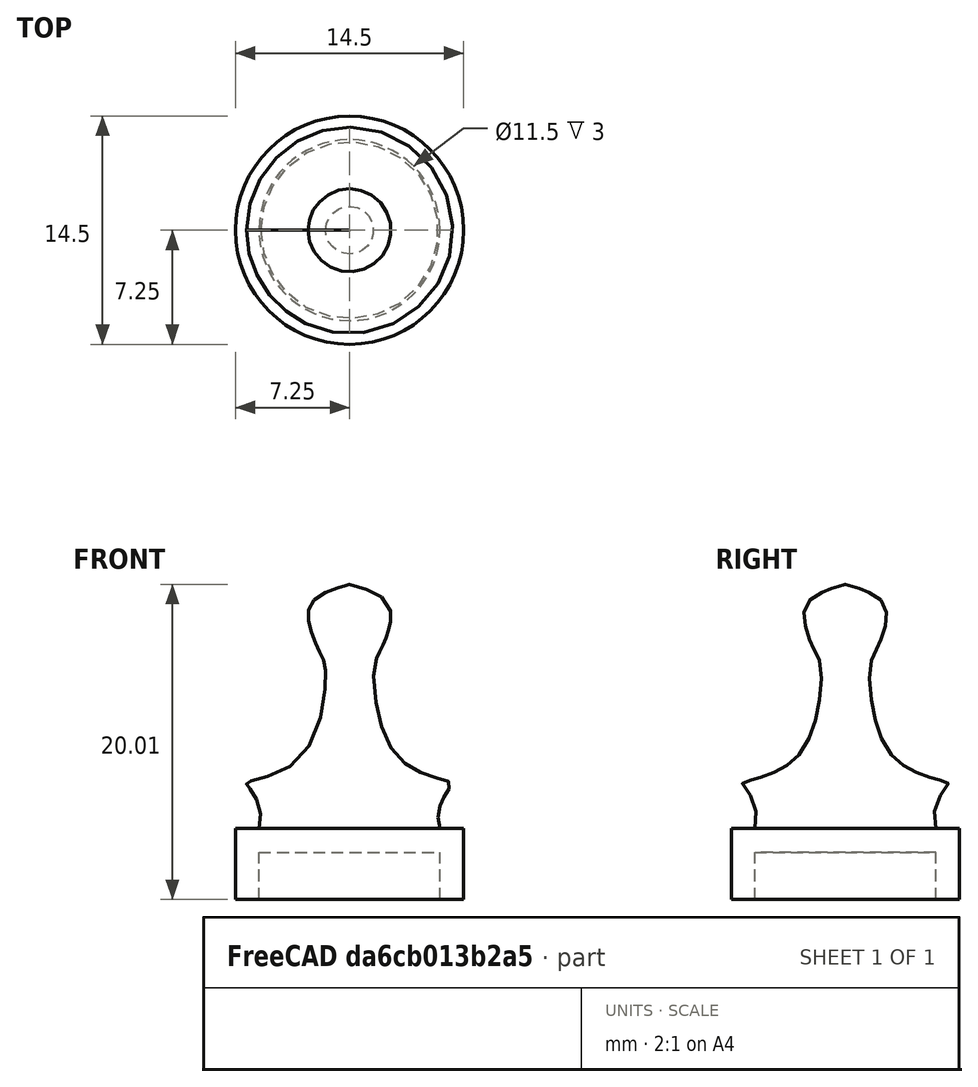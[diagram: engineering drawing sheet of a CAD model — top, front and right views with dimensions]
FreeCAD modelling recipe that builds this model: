
FCSTD DOCUMENT  (FreeCAD 0.21R33771 (Git))
Label: population unit
License: All rights reserved
LicenseURL: http://en.wikipedia.org/wiki/All_rights_reserved
objects: Sketcher::SketchObject×1, PartDesign::Revolution×1, PartDesign::Body×1
note: 4 computed .brp shape members not serialized (recipe doc carries the construction recipe); baked Part::Feature solids carry a one-line shape summary decoded from their .brp

FEATURE [Sketcher::SketchObject] Sketch
  FullyConstrained = false
  MapMode = 5
  Placement = pos=(0,0,0) rot=(1,0,0;1.5708rad)
  Support = -> [XZ_Plane]
  sketch-geometry (29):
    g0: LineSegment StartX=-5.75 StartY=0 StartZ=0 EndX=-5.75 EndY=3 EndZ=0
    g1: LineSegment StartX=-5.75 StartY=3 StartZ=0 EndX=0 EndY=3 EndZ=0
    g2: LineSegment StartX=-5.75 StartY=0 StartZ=0 EndX=-7.25 EndY=0 EndZ=0
    g3: LineSegment StartX=-7.25 StartY=0 StartZ=0 EndX=-7.25 EndY=4.5 EndZ=0
    g4: LineSegment StartX=-7.25 StartY=4.5 StartZ=0 EndX=-5.75 EndY=4.5 EndZ=0
    g5-g16: Circle x12 (B-spline internal-alignment scaffolding for g17; pole/knot coordinates omitted)
    g17: BSplineCurve PolesCount=12 KnotsCount=10 Degree=3 IsPeriodic=0
    g18-g27: GeomPoint x10 (B-spline internal-alignment scaffolding for g17; pole/knot coordinates omitted)
    g28: LineSegment StartX=0 StartY=20 StartZ=0 EndX=0 EndY=3 EndZ=0
  constraints (39):
    c: PointOnObject(g0,g-1)
    c: Vertical(g0)
    c: DistanceY(g0,g0) = 3
    c: Coincident(g1,g0)
    c: PointOnObject(g1,g-2)
    c: Horizontal(g1)
    c: DistanceX(g1,g1) = 5.75
    c: Coincident(g2,g0)
    c: PointOnObject(g2,g-1)
    c: DistanceX(g2,g2) = 1.5
    c: Coincident(g3,g2)
    c: Vertical(g3)
    c: DistanceY(g3,g3) = 4.5
    c: Coincident(g4,g3)
    c: Horizontal(g4)
    c: DistanceX(g4,g4) = 1.5
    c: Weight(g5) = 1
    c: Coincident(g17,g4)
    c: Equal(g5,g6)
    c: Equal(g5,g7)
    c: Equal(g5,g8)
    c: PointOnObject(g8,g7)
    c: Equal(g5,g9)
    c: Equal(g5,g10)
    c: Equal(g5,g11)
    c: PointOnObject(g11,g10)
    c: Equal(g5,g12)
    c: Equal(g5,g13)
    c: Equal(g5,g14)
    c: PointOnObject(g14,g-2)
    c: Equal(g5,g15)
    c: Coincident(g15,g14)
    c: Equal(g5,g16)
    c: InternalAlignment(g5-g16 -> g17) x12
    c: InternalAlignment(g18-g27 -> g17) x10
    c: Coincident(g28,g17)
    c: Coincident(g28,g1)
    c: Vertical(g28)
    c: DistanceY(g28,g28) = 17
FEATURE [PartDesign::Revolution] Revolution
  Angle = 360
  Axis = (0,-2e-16,1)
  Base = (0,0,0)
  Placement = pos=(0,0,0) rot=(1,0,0;1.5708rad)
  Profile = -> Sketch
  ReferenceAxis = -> Sketch [V_Axis]
FEATURE [PartDesign::Body] Body
  Group = -> [Sketch,Revolution]
  Origin = -> Origin
  Tip = -> Revolution
